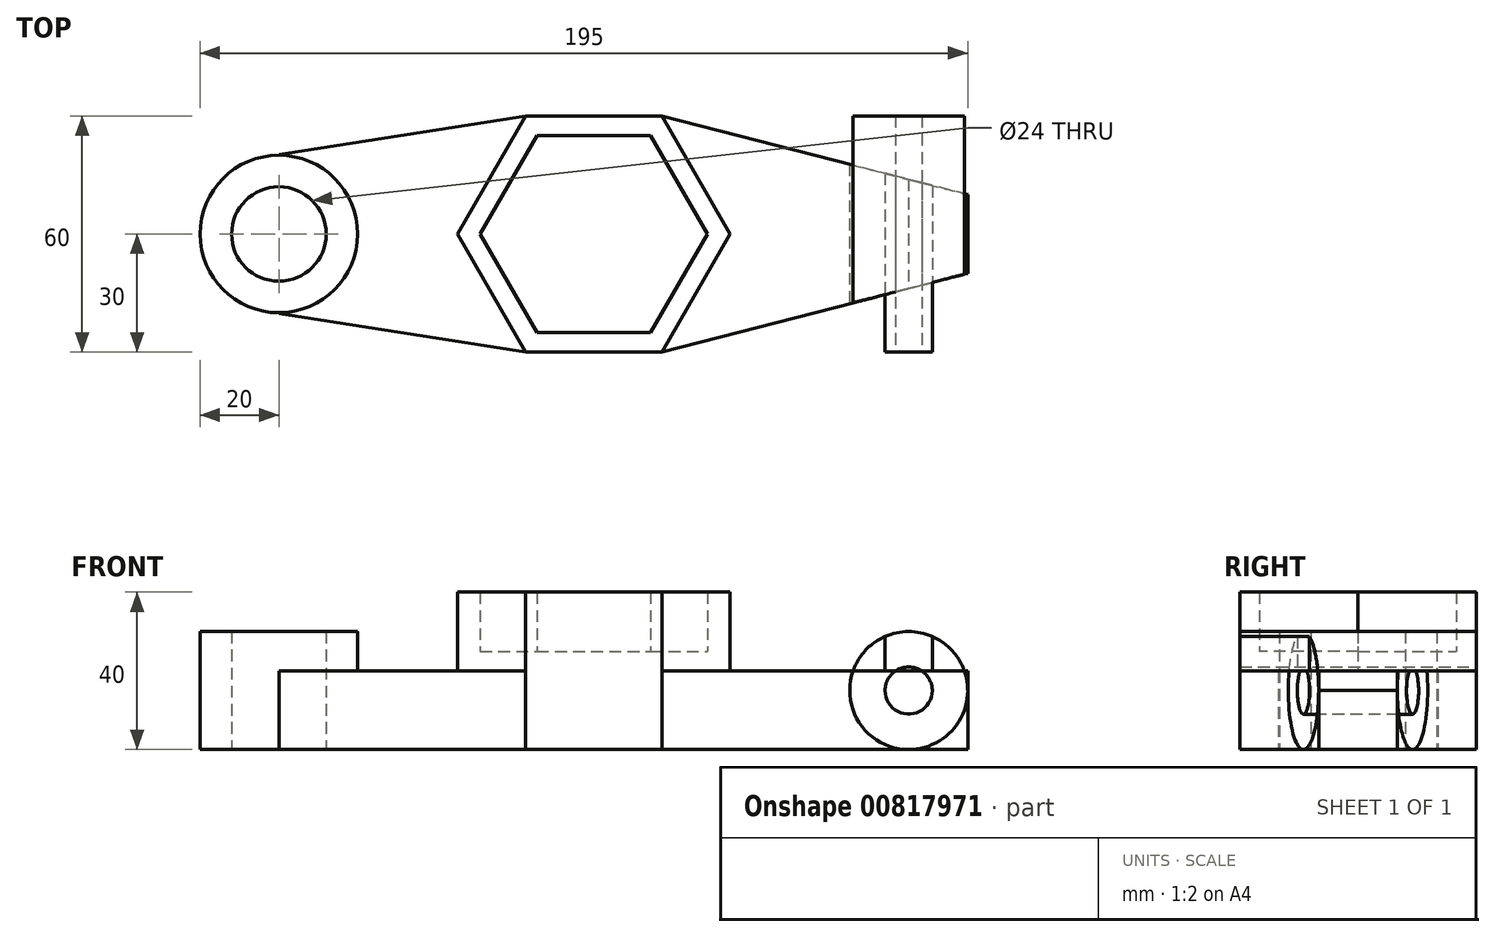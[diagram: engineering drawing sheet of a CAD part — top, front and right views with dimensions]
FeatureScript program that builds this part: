
annotation { "Feature Type Name" : "Feature", "Feature Type Description" : "" }
export const myFeature = defineFeature(function(context is Context, id is Id, definition is map)
    precondition{}
    {
        {
            var Q0;
            Q0=qCreatedBy(makeId("Top.planeOp"),FACE);
            var sketch = newSketch(context, id + "F0", { "sketchPlane" : qUnion([Q0])});
            skLineSegment(sketch, "E0.0", {"start": v(-17.32, 30) * mm, "end": v(17.32, 30) * mm});
            skLineSegment(sketch, "E0.1", {"start": v(17.32, 30) * mm, "end": v(34.64, 0) * mm});
            skLineSegment(sketch, "E0.2", {"start": v(34.64, 0) * mm, "end": v(17.32, -30) * mm});
            skLineSegment(sketch, "E0.3", {"start": v(17.32, -30) * mm, "end": v(-17.32, -30) * mm});
            skLineSegment(sketch, "E0.4", {"start": v(-17.32, -30) * mm, "end": v(-34.64, 0) * mm});
            skLineSegment(sketch, "E0.5", {"start": v(-34.64, 0) * mm, "end": v(-17.32, 30) * mm});
            skPoint(sketch, "E0.0.midPoint", {"position": v(0, 30) * mm});
            skLineSegment(sketch, "E1.0", {"start": v(-14.43, 25) * mm, "end": v(14.43, 25) * mm});
            skLineSegment(sketch, "E1.1", {"start": v(14.43, 25) * mm, "end": v(28.87, 0) * mm});
            skLineSegment(sketch, "E1.2", {"start": v(28.87, 0) * mm, "end": v(14.43, -25) * mm});
            skLineSegment(sketch, "E1.3", {"start": v(14.43, -25) * mm, "end": v(-14.43, -25) * mm});
            skLineSegment(sketch, "E1.4", {"start": v(-14.43, -25) * mm, "end": v(-28.87, 0) * mm});
            skLineSegment(sketch, "E1.5", {"start": v(-28.87, 0) * mm, "end": v(-14.43, 25) * mm});
            skPoint(sketch, "E1.0.midPoint", {"position": v(0, 25) * mm});
            skPoint(sketch, "E1.cCircle.center.orphan", {"position": v(0, 0) * mm});
            skLineSegment(sketch, "E2", {"start": v(0, -30) * mm, "end": v(17.32, -30) * mm});
            skLineSegment(sketch, "E3", {"start": v(80, -30) * mm, "end": v(-80, -30) * mm});
            skLineSegment(sketch, "E4", {"start": v(-80, -30) * mm, "end": v(-80, 77.5) * mm});
            skLineSegment(sketch, "E5", {"start": v(-80, 77.5) * mm, "end": v(80, 74.97) * mm});
            skLineSegment(sketch, "E6", {"start": v(80, 10) * mm, "end": v(80, -10) * mm});
            skCircle(sketch, "E7", {"center": v(-80, 0) * mm, "radius": 20 * mm});
            skCircle(sketch, "E8", {"center": v(-80, 0) * mm, "radius": 12 * mm});
            skLineSegment(sketch, "E9", {"start": v(-94.69, -53.3) * mm, "end": v(-133.8, -5.86) * mm});
            skLineSegment(sketch, "E10", {"start": v(-131.36, 27.39) * mm, "end": v(-93.95, 59.42) * mm});
            skLineSegment(sketch, "E11", {"start": v(-17.32, -30) * mm, "end": v(-80, -20.24) * mm});
            skLineSegment(sketch, "E12", {"start": v(-17.32, 30) * mm, "end": v(-80, 20.24) * mm});
            skPoint(sketch, "E13.center.orphan", {"position": v(80, 0) * mm});
            skLineSegment(sketch, "E14", {"start": v(80, 0) * mm, "end": v(80, 10) * mm});
            skLineSegment(sketch, "E15", {"start": v(74, -10) * mm, "end": v(74, 10) * mm});
            skLineSegment(sketch, "E16", {"start": v(86, 10) * mm, "end": v(86, -10) * mm});
            skLineSegment(sketch, "E17", {"start": v(80, -30) * mm, "end": v(95, -30) * mm});
            skLineSegment(sketch, "E18", {"start": v(95, -30) * mm, "end": v(95, 74.97) * mm});
            skLineSegment(sketch, "E19", {"start": v(95, 74.97) * mm, "end": v(80, 74.97) * mm});
            skLineSegment(sketch, "E20", {"start": v(17.32, -30) * mm, "end": v(95, -10) * mm});
            skLineSegment(sketch, "E21", {"start": v(95, -10) * mm, "end": v(95, 10) * mm});
            skLineSegment(sketch, "E22", {"start": v(95, 10) * mm, "end": v(17.32, 30) * mm});
            skLineSegment(sketch, "E23", {"start": v(86, -10) * mm, "end": v(86, -30) * mm});
            skLineSegment(sketch, "E24", {"start": v(86, -30) * mm, "end": v(74, -30) * mm});
            skLineSegment(sketch, "E25", {"start": v(74, -30) * mm, "end": v(74, -10) * mm});
            skLineSegment(sketch, "E26", {"start": v(74, -30) * mm, "end": v(74, 30) * mm});
            skLineSegment(sketch, "E27", {"start": v(74, 30) * mm, "end": v(86, 30) * mm});
            skLineSegment(sketch, "E28", {"start": v(86, 30) * mm, "end": v(86, 10) * mm});
            skSolve(sketch);
        }
        {
            var Q0;
            Q0=makeQuery(id+"F0.imprint","IMPRINT",FACE,{"disambiguationData":[TD([[makeQuery(id+"F0.imprint","IMPRINT",EDGE,{"derivedFrom":sQuery(id+"F0.wireOp",EDGE,"E0.0")}),-1.0]])]});
            extrude(context, id + "F1", {"entities" : qUnion([Q0]), "depth" : 40 * mm, "offsetDistance" : 25 * mm});
        }
        {
            var Q0;
            Q0=makeQuery(id+"F0.imprint","IMPRINT",FACE,{"disambiguationData":[TD([[makeQuery(id+"F0.imprint","IMPRINT",EDGE,{"derivedFrom":sQuery(id+"F0.wireOp",EDGE,"E1.0")}),-1.0]])]});
            extrude(context, id + "F2", {"entities" : qUnion([Q0]), "operationType" : NewBodyOperationType.ADD, "depth" : 25 * mm, "offsetDistance" : 25 * mm});
        }
        {
            var Q0;
            Q0=makeQuery(id+"F0.imprint","IMPRINT",FACE,{"disambiguationData":[TD([[makeQuery(id+"F0.imprint","IMPRINT",EDGE,{"derivedFrom":sQuery(id+"F0.wireOp",EDGE,"E0.1")}),1.0]])]});
            var Q1;
            Q1=makeQuery(id+"F0.imprint","IMPRINT",FACE,{"disambiguationData":[TD([[makeQuery(id+"F0.imprint","IMPRINT",EDGE,{"derivedFrom":sQuery(id+"F0.wireOp",EDGE,"E0.4")}),1.0]])]});
            extrude(context, id + "F3", {"entities" : qUnion([Q0, Q1]), "operationType" : NewBodyOperationType.ADD, "depth" : 20 * mm, "offsetDistance" : 25 * mm});
        }
        {
            var Q0;
            {var subQ1=sQuery(id+"F0.wireOp",EDGE,"E16");Q0=makeQuery(id+"F0.imprint","IMPRINT",FACE,{"disambiguationData":[TD([[makeQuery(id+"F0.imprint","IMPRINT",EDGE,{"derivedFrom":subQ1}),-1.0]])]});}
            var Q1;
            {var subQ8=sQuery(id+"F0.wireOp",EDGE,"E16");Q1=makeQuery(id+"F0.imprint","IMPRINT",FACE,{"disambiguationData":[TD([[makeQuery(id+"F0.imprint","IMPRINT",EDGE,{"derivedFrom":subQ8}),1.0]])]});}
            extrude(context, id + "F4", {"entities" : qUnion([Q0, Q1]), "operationType" : NewBodyOperationType.ADD, "depth" : 20 * mm, "offsetDistance" : 25 * mm});
        }
        {
            var Q0;
            {var subQ0=sQuery(id+"F0.wireOp",EDGE,"E7");var subQ1=sQuery(id+"F0.wireOp",EDGE,"E4");var subQ2=makeQuery(id+"F0.imprint","INTERSECT",VERTEX,{"disambiguationData":[OD(0.0)],"derivedFrom":[subQ1,subQ0]});Q0=makeQuery(id+"F0.imprint","IMPRINT",FACE,{"disambiguationData":[TD([[makeQuery(id+"F0.imprint","IMPRINT",EDGE,{"disambiguationData":[TD([[subQ2,-1.0]])],"derivedFrom":subQ1}),-1.0]])]});}
            var Q1;
            {var subQ0=sQuery(id+"F0.wireOp",EDGE,"E7");var subQ1=sQuery(id+"F0.wireOp",EDGE,"E4");var subQ2=makeQuery(id+"F0.imprint","INTERSECT",VERTEX,{"disambiguationData":[OD(0.0)],"derivedFrom":[subQ1,subQ0]});Q1=makeQuery(id+"F0.imprint","IMPRINT",FACE,{"disambiguationData":[TD([[makeQuery(id+"F0.imprint","IMPRINT",EDGE,{"disambiguationData":[TD([[subQ2,-1.0]])],"derivedFrom":subQ1}),1.0]])]});}
            extrude(context, id + "F5", {"entities" : qUnion([Q0, Q1]), "operationType" : NewBodyOperationType.ADD, "depth" : 30 * mm, "offsetDistance" : 25 * mm});
        }
        {
            var Q0;
            Q0=qCreatedBy(makeId("Front.planeOp"),FACE);
            var sketch = newSketch(context, id + "F6", { "sketchPlane" : qUnion([Q0])});
            skLineSegment(sketch, "E29.0.0", {"start": v(17.32, 0) * mm, "end": v(95, 0) * mm});
            skLineSegment(sketch, "E29.0.1", {"start": v(95, 0) * mm, "end": v(95, 20) * mm});
            skLineSegment(sketch, "E29.0.2", {"start": v(95, 20) * mm, "end": v(17.32, 20) * mm});
            skLineSegment(sketch, "E29.0.3", {"start": v(17.32, 20) * mm, "end": v(17.32, 0) * mm});
            skLineSegment(sketch, "E30", {"start": v(95, 0) * mm, "end": v(95, 10) * mm});
            skLineSegment(sketch, "E31", {"start": v(95, 0) * mm, "end": v(95, 15) * mm});
            skLineSegment(sketch, "E32", {"start": v(95, 15) * mm, "end": v(80, 15) * mm});
            skCircle(sketch, "E33", {"center": v(80, 15) * mm, "radius": 6 * mm});
            skCircle(sketch, "E34", {"center": v(80, 15) * mm, "radius": 15 * mm});
            skSolve(sketch);
        }
        {
            var Q0;
            {var subQ0=sQuery(id+"F6.wireOp",EDGE,"E34");var subQ6=sQuery(id+"F6.wireOp",EDGE,"E29.0.2");var subQ8=makeQuery(id+"F6.imprint","INTERSECT",VERTEX,{"disambiguationData":[OD(0.0)],"derivedFrom":[subQ6,subQ0]});Q0=makeQuery(id+"F6.imprint","IMPRINT",FACE,{"disambiguationData":[TD([[makeQuery(id+"F6.imprint","IMPRINT",EDGE,{"disambiguationData":[TD([[subQ8,1.0]])],"derivedFrom":subQ6}),1.0]])]});}
            var Q1;
            {var subQ0=sQuery(id+"F6.wireOp",EDGE,"E34");var subQ1=sQuery(id+"F6.wireOp",EDGE,"E29.0.2");var subQ2=makeQuery(id+"F6.imprint","INTERSECT",VERTEX,{"disambiguationData":[OD(0.0)],"derivedFrom":[subQ1,subQ0]});Q1=makeQuery(id+"F6.imprint","IMPRINT",FACE,{"disambiguationData":[TD([[makeQuery(id+"F6.imprint","IMPRINT",EDGE,{"disambiguationData":[TD([[subQ2,1.0]])],"derivedFrom":subQ1}),-1.0]])]});}
            var Q2;
            {var subQ0=sQuery(id+"F6.wireOp",EDGE,"E34");var subQ1=sQuery(id+"F6.wireOp",EDGE,"E29.0.2");var subQ2=makeQuery(id+"F6.imprint","INTERSECT",VERTEX,{"disambiguationData":[OD(1.0)],"derivedFrom":[subQ1,subQ0]});Q2=makeQuery(id+"F6.imprint","IMPRINT",FACE,{"disambiguationData":[TD([[makeQuery(id+"F6.imprint","IMPRINT",EDGE,{"disambiguationData":[TD([[subQ2,-1.0]])],"derivedFrom":subQ1}),1.0]])]});}
            extrude(context, id + "F7", {"entities" : qUnion([Q0, Q1, Q2]), "depth" : 30 * mm, "offsetDistance" : 25 * mm, "hasSecondDirection" : true, "secondDirectionOppositeDirection" : true, "secondDirectionDepth" : 30 * mm});
        }
        {
            var Q0;
            Q0=makeQuery(id+"F7.opExtrude","CAP_FACE",FACE,{"disambiguationData":[OSD([sQuery(id+"F6.wireOp",EDGE,"E33"),sQuery(id+"F6.wireOp",EDGE,"E34")])],"isStart":false});
            var sketch = newSketch(context, id + "F8", { "sketchPlane" : qUnion([Q0])});
            skLineSegment(sketch, "E35.0.0", {"start": v(17.32, 0) * mm, "end": v(95, 0) * mm});
            skLineSegment(sketch, "E35.0.1", {"start": v(95, 0) * mm, "end": v(95, 20) * mm});
            skLineSegment(sketch, "E35.0.2", {"start": v(95, 20) * mm, "end": v(17.32, 20) * mm});
            skLineSegment(sketch, "E35.0.3", {"start": v(17.32, 20) * mm, "end": v(17.32, 0) * mm});
            skCircle(sketch, "E36.0", {"center": v(80, 15) * mm, "radius": 6 * mm});
            skSolve(sketch);
        }
        {
            var Q0;
            {var subQ0=sQuery(id+"F8.wireOp",EDGE,"E36.0");var subQ1=sQuery(id+"F8.wireOp",EDGE,"E35.0.2");var subQ2=makeQuery(id+"F8.imprint","INTERSECT",VERTEX,{"disambiguationData":[OD(0.0)],"derivedFrom":[subQ1,subQ0]});Q0=makeQuery(id+"F8.imprint","IMPRINT",FACE,{"disambiguationData":[TD([[makeQuery(id+"F8.imprint","IMPRINT",EDGE,{"disambiguationData":[TD([[subQ2,-1.0]])],"derivedFrom":subQ1}),1.0]])]});}
            extrude(context, id + "F9", {"entities" : qUnion([Q0]), "operationType" : NewBodyOperationType.REMOVE, "oppositeDirection" : true, "depth" : 70.8 * mm, "offsetDistance" : 25 * mm});
        }
        {
            var Q0;
            Q0=qCreatedBy(makeId("Top.planeOp"),FACE);
            var sketch = newSketch(context, id + "F10", { "sketchPlane" : qUnion([Q0])});
            skLineSegment(sketch, "E37.0", {"start": v(86, 10) * mm, "end": v(86, -10) * mm});
            skLineSegment(sketch, "E37.1", {"start": v(80, -30) * mm, "end": v(-80, -30) * mm});
            skLineSegment(sketch, "E37.2", {"start": v(-17.32, 30) * mm, "end": v(17.32, 30) * mm});
            skLineSegment(sketch, "E37.3", {"start": v(17.32, 30) * mm, "end": v(34.64, 0) * mm});
            skLineSegment(sketch, "E37.4", {"start": v(34.64, 0) * mm, "end": v(17.32, -30) * mm});
            skLineSegment(sketch, "E37.5", {"start": v(-14.43, 25) * mm, "end": v(14.43, 25) * mm});
            skLineSegment(sketch, "E37.6", {"start": v(14.43, 25) * mm, "end": v(28.87, 0) * mm});
            skLineSegment(sketch, "E37.7", {"start": v(28.87, 0) * mm, "end": v(14.43, -25) * mm});
            skLineSegment(sketch, "E37.8", {"start": v(14.43, -25) * mm, "end": v(-14.43, -25) * mm});
            skLineSegment(sketch, "E37.9", {"start": v(0, -30) * mm, "end": v(17.32, -30) * mm});
            skLineSegment(sketch, "E37.10", {"start": v(80, -30) * mm, "end": v(95, -30) * mm});
            skLineSegment(sketch, "E37.11", {"start": v(74, -30) * mm, "end": v(74, 30) * mm});
            skLineSegment(sketch, "E37.12", {"start": v(95, 10) * mm, "end": v(17.32, 30) * mm});
            skLineSegment(sketch, "E37.13", {"start": v(95, -30) * mm, "end": v(95, 74.97) * mm});
            skLineSegment(sketch, "E37.14", {"start": v(80, 10) * mm, "end": v(80, -10) * mm});
            skLineSegment(sketch, "E37.15", {"start": v(17.32, -30) * mm, "end": v(95, -10) * mm});
            skLineSegment(sketch, "E37.16", {"start": v(74, 30) * mm, "end": v(86, 30) * mm});
            skLineSegment(sketch, "E37.17", {"start": v(86, -10) * mm, "end": v(86, -30) * mm});
            skLineSegment(sketch, "E37.18", {"start": v(74, -10) * mm, "end": v(74, 10) * mm});
            skLineSegment(sketch, "E37.19", {"start": v(86, 30) * mm, "end": v(86, 10) * mm});
            skLineSegment(sketch, "E37.20", {"start": v(95, -10) * mm, "end": v(95, 10) * mm});
            skLineSegment(sketch, "E37.21", {"start": v(86, -30) * mm, "end": v(74, -30) * mm});
            skLineSegment(sketch, "E37.22", {"start": v(95, 30) * mm, "end": v(65, 30) * mm});
            skLineSegment(sketch, "E37.23", {"start": v(17.32, -30) * mm, "end": v(-17.32, -30) * mm});
            skLineSegment(sketch, "E37.24", {"start": v(80, 0) * mm, "end": v(80, 10) * mm});
            skPoint(sketch, "E38.0", {"position": v(17.32, -30) * mm});
            skPoint(sketch, "E39.0", {"position": v(95, -10) * mm});
            skLineSegment(sketch, "E40", {"start": v(17.32, -30) * mm, "end": v(95, -30) * mm});
            skLineSegment(sketch, "E41", {"start": v(95, -10) * mm, "end": v(95, -30) * mm});
            skLineSegment(sketch, "E42", {"start": v(95, -10) * mm, "end": v(17.32, -30) * mm});
            skSolve(sketch);
        }
        {
            var Q0;
            {var subQ0=sQuery(id+"F0.wireOp",EDGE,"E20");var subQ3=sQuery(id+"F0.wireOp",EDGE,"E26");var subQ5=makeQuery(id+"F0.imprint","INTERSECT",VERTEX,{"derivedFrom":[subQ0,subQ3]});Q0=makeQuery(id+"F0.imprint","IMPRINT",FACE,{"disambiguationData":[TD([[makeQuery(id+"F0.imprint","IMPRINT",EDGE,{"disambiguationData":[TD([[subQ5,1.0]])],"derivedFrom":subQ0}),-1.0]])]});}
            var Q1;
            {var subQ5=sQuery(id+"F0.wireOp",EDGE,"E24");Q1=makeQuery(id+"F0.imprint","IMPRINT",FACE,{"disambiguationData":[TD([[makeQuery(id+"F0.imprint","IMPRINT",EDGE,{"derivedFrom":subQ5}),-1.0]])]});}
            var Q2;
            {var subQ0=sQuery(id+"F0.wireOp",EDGE,"E17");Q2=makeQuery(id+"F0.imprint","IMPRINT",FACE,{"disambiguationData":[TD([[makeQuery(id+"F0.imprint","IMPRINT",EDGE,{"derivedFrom":subQ0}),1.0]])]});}
            extrude(context, id + "F11", {"entities" : qUnion([Q0, Q1, Q2]), "operationType" : NewBodyOperationType.REMOVE, "depth" : 43.2 * mm, "offsetDistance" : 25 * mm});
        }
    });
